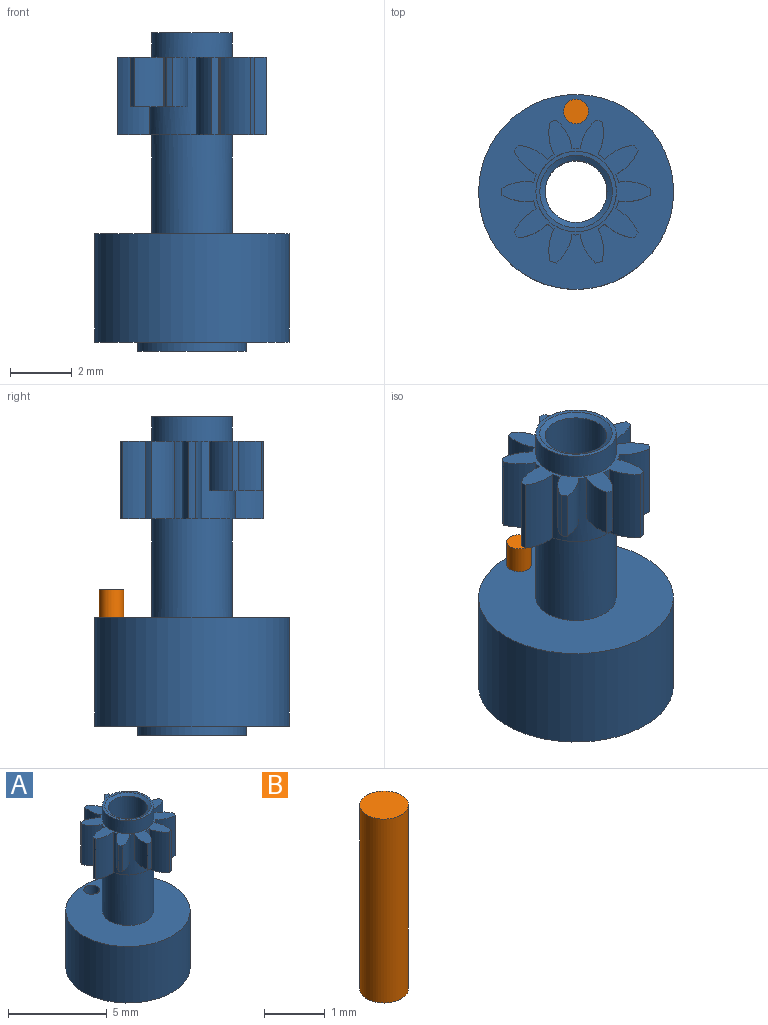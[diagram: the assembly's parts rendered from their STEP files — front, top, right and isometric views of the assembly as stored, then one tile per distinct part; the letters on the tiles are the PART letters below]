
ASSEMBLY  parts=2 mates=1
PART A: 54 faces, bbox 6.3x6.3x10.3 mm
  f0: plane 4.8x4.63mm, normal (0,0,-1), area 5.2mm2, adj f1,f8,f9,f10,f11,f12,f13,f14
  f1: cylinder r=1.5mm len=2.5mm, axis (0,0,-1), area 2.7mm2, adj f0,f8,f38,f39
  f2: cylinder r=1.5mm len=1.6mm, axis (0,0,-1), area 1.7mm2, adj f3,f8,f39,f40
  f3: cylinder r=2.4mm len=1.6mm, axis (0,0,-1), area 0.3mm2, adj f2,f4,f39,f40
  f4: cylinder r=1.5mm len=1.6mm, axis (0,0,-1), area 1.7mm2, adj f3,f8,f39,f40
  f5: cylinder r=1.5mm len=1.6mm, axis (0,0,-1), area 1.7mm2, adj f6,f8,f39,f41
  f6: cylinder r=2.4mm len=1.6mm, axis (0,0,-1), area 0.3mm2, adj f5,f7,f39,f41
  f7: cylinder r=1.5mm len=1.6mm, axis (0,0,-1), area 1.7mm2, adj f6,f8,f39,f41
  f8: cylinder r=1.4mm len=2.5mm, axis (0,0,-1), area 3.1mm2, adj f0,f1,f2,f4,f5,f7,f9,f39
  f9: cylinder r=1.5mm len=2.5mm, axis (0,0,-1), area 2.7mm2, adj f0,f8,f10,f39
  f10: cylinder r=2.4mm len=2.5mm, axis (0,0,-1), area 0.5mm2, adj f0,f9,f11,f39
  f11: cylinder r=1.5mm len=2.5mm, axis (0,0,-1), area 2.7mm2, adj f0,f10,f12,f39
  f12: cylinder r=1.4mm len=2.5mm, axis (0,0,-1), area 0.7mm2, adj f0,f11,f13,f39
  f13: cylinder r=1.5mm len=2.5mm, axis (0,0,-1), area 2.7mm2, adj f0,f12,f14,f39
  f14: cylinder r=2.4mm len=2.5mm, axis (0,0,-1), area 0.5mm2, adj f0,f13,f15,f39
  f15: cylinder r=1.5mm len=2.5mm, axis (0,0,-1), area 2.7mm2, adj f0,f14,f16,f39
  f16: cylinder r=1.4mm len=2.5mm, axis (0,0,-1), area 0.7mm2, adj f0,f15,f17,f39
  f17: cylinder r=1.5mm len=2.5mm, axis (0,0,-1), area 2.7mm2, adj f0,f16,f18,f39
  f18: cylinder r=2.4mm len=2.5mm, axis (0,0,-1), area 0.5mm2, adj f0,f17,f19,f39
  f19: cylinder r=1.5mm len=2.5mm, axis (0,0,-1), area 2.7mm2, adj f0,f18,f20,f39
  f20: cylinder r=1.4mm len=2.5mm, axis (0,0,-1), area 0.7mm2, adj f0,f19,f21,f39
  f21: cylinder r=1.5mm len=2.5mm, axis (0,0,-1), area 2.7mm2, adj f0,f20,f22,f39
  f22: cylinder r=2.4mm len=2.5mm, axis (0,0,-1), area 0.5mm2, adj f0,f21,f23,f39
  f23: cylinder r=1.5mm len=2.5mm, axis (0,0,-1), area 2.7mm2, adj f0,f22,f24,f39
  f24: cylinder r=1.4mm len=2.5mm, axis (0,0,-1), area 0.7mm2, adj f0,f23,f25,f39
  f25: cylinder r=1.5mm len=2.5mm, axis (0,0,-1), area 2.7mm2, adj f0,f24,f26,f39
  f26: cylinder r=2.4mm len=2.5mm, axis (0,0,-1), area 0.5mm2, adj f0,f25,f27,f39
  f27: cylinder r=1.5mm len=2.5mm, axis (0,0,-1), area 2.7mm2, adj f0,f26,f28,f39
  f28: cylinder r=1.4mm len=2.5mm, axis (0,0,-1), area 0.7mm2, adj f0,f27,f29,f39
  f29: cylinder r=1.5mm len=2.5mm, axis (0,0,-1), area 2.7mm2, adj f0,f28,f30,f39
  f30: cylinder r=2.4mm len=2.5mm, axis (0,0,-1), area 0.5mm2, adj f0,f29,f31,f39
  f31: cylinder r=1.5mm len=2.5mm, axis (0,0,-1), area 2.7mm2, adj f0,f30,f32,f39
  f32: cylinder r=1.4mm len=2.5mm, axis (0,0,-1), area 0.7mm2, adj f0,f31,f33,f39
  f33: cylinder r=1.5mm len=2.5mm, axis (0,0,-1), area 2.7mm2, adj f0,f32,f34,f39
  f34: cylinder r=2.4mm len=2.5mm, axis (0,0,-1), area 0.5mm2, adj f0,f33,f35,f39
  f35: cylinder r=1.5mm len=2.5mm, axis (0,0,-1), area 2.7mm2, adj f0,f34,f36,f39
  f36: cylinder r=1.4mm len=2.5mm, axis (0,0,-1), area 0.7mm2, adj f0,f35,f37,f39
  f37: cylinder r=1.5mm len=2.5mm, axis (0,0,-1), area 2.7mm2, adj f0,f36,f38,f39
  f38: cylinder r=2.4mm len=2.5mm, axis (0,0,-1), area 0.5mm2, adj f0,f1,f37,f39
  f39: plane 4.8x4.63mm, normal (0,0,1), area 6.3mm2, adj f1,f2,f3,f4,f5,f6,f7,f8
  f40: plane 1.07x0.94mm, normal (0,0,-1), area 0.5mm2, adj f2,f3,f4,f8
  f41: plane 1.11x0.75mm, normal (0,0,-1), area 0.5mm2, adj f5,f6,f7,f8
  f42: cylinder r=1.3mm len=3.2mm, axis (0,0,-1), area 26.1mm2, adj f0,f49
  f43: cylinder r=1mm len=9.51mm, axis (0,0,-1), area 59.7mm2, adj f44,f53
  f44: cone r=1mm half-angle=30deg, axis (0,0,-1), area 6mm2, adj f43,f45
  f45: plane 3.5x3.5mm, normal (0,0,-1), area 3.5mm2, adj f44,f46
  f46: cylinder r=1.75mm len=3.5mm, axis (0,0,-1), area 3.3mm2, adj f45,f47
  f47: plane 6.3x6.3mm, normal (0,0,-1), area 21mm2, adj f46,f48,f52
  f48: cylinder r=3.15mm len=6.3mm, axis (0,0,-1), area 69.3mm2, adj f47,f49
  f49: plane 6.3x6.3mm, normal (0,0,1), area 25.4mm2, adj f42,f48,f52
  f50: cylinder r=1.3mm len=2.6mm, axis (0,0,-1), area 6.5mm2, adj f39,f51
  f51: plane 2.6x2.6mm, normal (0,0,1), area 1mm2, adj f50,f53
  f52: cylinder r=0.4mm len=3.5mm, axis (0,0,1), area 8.8mm2, adj f47,f49
  f53: cone r=1.17mm half-angle=60deg, axis (0,0,1), area 1.4mm2, adj f43,f51
PART B: 3 faces, bbox 0.8x0.8x3.7 mm
  f0: cylinder r=0.4mm len=3.7mm, axis (0,0,-1), area 9.3mm2, adj f1,f2
  f1: plane 0.8x0.8mm, normal (0,0,1), area 0.5mm2, adj f0
  f2: plane 0.8x0.8mm, normal (0,0,-1), area 0.5mm2, adj f0
PLACE A at identity
PLACE B t=(0,2.6,1)mm
MATE fastened B.f0 <-> A.f52  axis (0,0,1) through (0,2.6,4.7)mm
